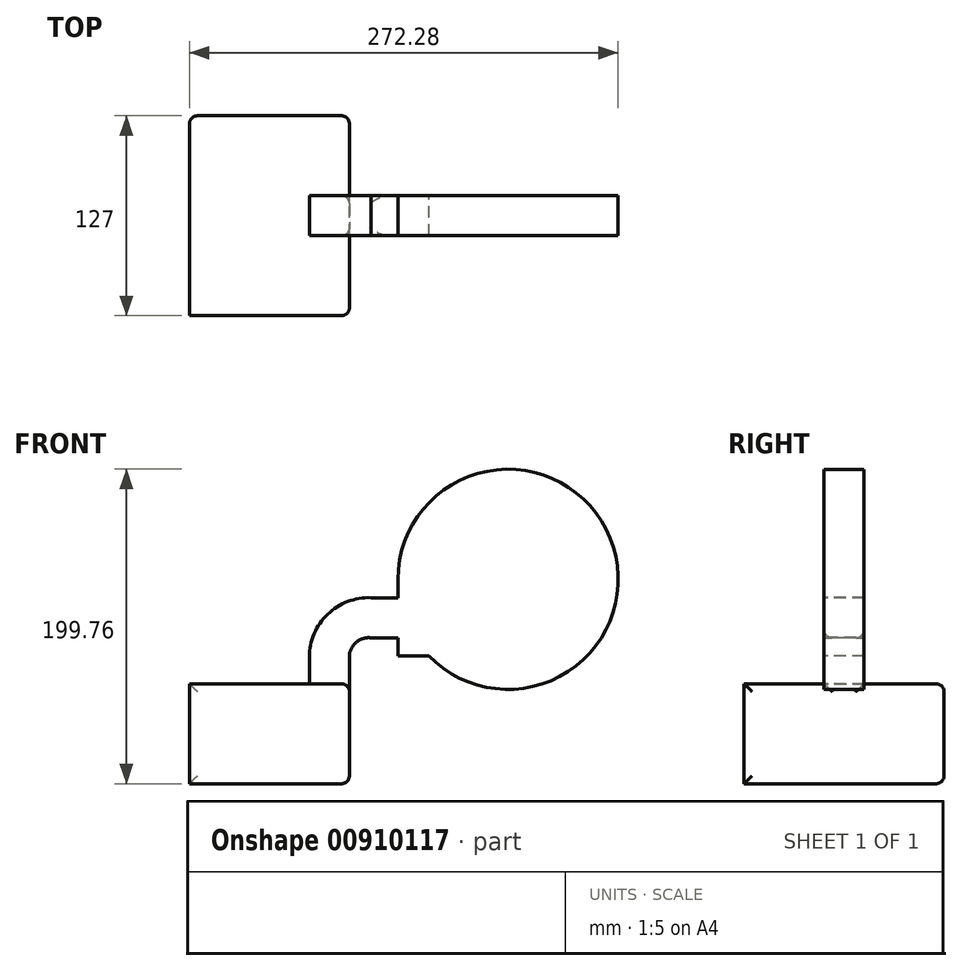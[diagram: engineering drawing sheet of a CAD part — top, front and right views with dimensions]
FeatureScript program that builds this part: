
annotation { "Feature Type Name" : "Feature", "Feature Type Description" : "" }
export const myFeature = defineFeature(function(context is Context, id is Id, definition is map)
    precondition{}
    {
        {
            var Q0;
            Q0=qCreatedBy(makeId("Front.planeOp"),FACE);
            var sketch = newSketch(context, id + "F0", { "sketchPlane" : qUnion([Q0])});
            skLineSegment(sketch, "E0.bottom", {"start": v(-50.8, -31.75) * mm, "end": v(50.8, -31.75) * mm});
            skLineSegment(sketch, "E0.top", {"start": v(-50.8, 31.75) * mm, "end": v(50.8, 31.75) * mm});
            skLineSegment(sketch, "E0.left", {"start": v(-50.8, -31.75) * mm, "end": v(-50.8, 31.75) * mm});
            skLineSegment(sketch, "E0.right", {"start": v(50.8, -31.75) * mm, "end": v(50.8, 31.75) * mm});
            skPoint(sketch, "E0.middle", {"position": v(0, 0) * mm});
            skLineSegment(sketch, "E1.bottom", {"start": v(81.64, 98.09) * mm, "end": v(151.56, 98.09) * mm});
            skLineSegment(sketch, "E1.top", {"start": v(81.64, 49.56) * mm, "end": v(151.56, 49.56) * mm});
            skLineSegment(sketch, "E1.left", {"start": v(81.64, 98.09) * mm, "end": v(81.64, 49.56) * mm});
            skLineSegment(sketch, "E1.right", {"start": v(151.56, 98.09) * mm, "end": v(151.56, 49.56) * mm});
            skPoint(sketch, "E1.middle", {"position": v(116.6, 73.82) * mm});
            skLineSegment(sketch, "E2", {"start": v(50.8, 31.75) * mm, "end": v(50.8, 48.66) * mm});
            skArc(sketch, "E3", {"start": v(50.8, 48.66) * mm, "mid": v(54.72, 57.7) * mm, "end": v(64, 61) * mm});
            skLineSegment(sketch, "E4", {"start": v(64, 61) * mm, "end": v(113.1, 61) * mm});
            skLineSegment(sketch, "E5.0", {"start": v(64.63, 86.4) * mm, "end": v(113.1, 86.4) * mm});
            skArc(sketch, "E5.1", {"start": v(25.4, 48.66) * mm, "mid": v(36.99, 75.87) * mm, "end": v(64.63, 86.4) * mm});
            skLineSegment(sketch, "E5.2", {"start": v(25.4, 31.75) * mm, "end": v(25.4, 48.66) * mm});
            skFitSpline(sketch, "E6", {"points": [v(-50.8, 31.75) * mm, v(64.63, 86.4) * mm], "startDerivative": vector(115.43, 54.64) * mm, "endDerivative": vector(139.56, -16.4) * mm});
            skSolve(sketch);
        }
        {
            var Q0;
            Q0=makeQuery(id+"F0.imprint","IMPRINT",FACE,{"disambiguationData":[TD([[makeQuery(id+"F0.imprint","IMPRINT",EDGE,{"derivedFrom":sQuery(id+"F0.wireOp",EDGE,"E0.bottom")}),1.0]])]});
            extrude(context, id + "F1", {"entities" : qUnion([Q0]), "endBound" : BoundingType.SYMMETRIC, "depth" : 127 * mm, "offsetDistance" : 25.4 * mm});
        }
        {
            var Q0;
            Q0=makeQuery(id+"F0.imprint","IMPRINT",FACE,{"disambiguationData":[TD([[makeQuery(id+"F0.imprint","IMPRINT",EDGE,{"derivedFrom":sQuery(id+"F0.wireOp",EDGE,"E5.1")}),1.0]])]});
            var Q1;
            {var subQ0=sQuery(id+"F0.wireOp",EDGE,"E2");Q1=makeQuery(id+"F0.imprint","IMPRINT",FACE,{"disambiguationData":[TD([[makeQuery(id+"F0.imprint","IMPRINT",EDGE,{"derivedFrom":subQ0}),1.0]])]});}
            var Q2;
            {var subQ3=sQuery(id+"F0.wireOp",EDGE,"E1.bottom");Q2=makeQuery(id+"F0.imprint","IMPRINT",FACE,{"disambiguationData":[TD([[makeQuery(id+"F0.imprint","IMPRINT",EDGE,{"derivedFrom":subQ3}),-1.0]])]});}
            extrude(context, id + "F2", {"entities" : qUnion([Q0, Q1, Q2]), "operationType" : NewBodyOperationType.ADD, "endBound" : BoundingType.SYMMETRIC, "oppositeDirection" : true, "depth" : 25.4 * mm, "offsetDistance" : 25.4 * mm});
        }
        {
            var Q0;
            Q0=makeQuery(id+"F2.opExtrude","SWEPT_FACE",FACE,{"disambiguationData":[OSD([sQuery(id+"F0.wireOp",EDGE,"E1.bottom")])]});
            var Q1;
            Q1=makeQuery(id+"F2.opExtrude","SWEPT_EDGE",EDGE,{"disambiguationData":[OSD([sQuery(id+"F0.wireOp",EDGE,"E1.bottom"),sQuery(id+"F0.wireOp",EDGE,"E1.right")])]});
            revolve(context, id + "F3", {"operationType" : NewBodyOperationType.ADD, "surfaceOperationType" : NewSurfaceOperationType.NEW, "entities" : qUnion([Q0]), "axis" : qUnion([Q1]), "revolveType" : RevolveType.FULL});
        }
        {
            var Q0;
            Q0=makeQuery(id+"F2.boolean.opBoolean","MERGE",FACE,{"derivedFrom":[makeQuery(id+"F1.opExtrude","SWEPT_FACE",FACE,{"disambiguationData":[OSD([sQuery(id+"F0.wireOp",EDGE,"E0.right")])]}),makeQuery(id+"F2.opExtrude","SWEPT_FACE",FACE,{"disambiguationData":[OSD([sQuery(id+"F0.wireOp",EDGE,"E2")])]})]});
            var Q1;
            Q1=makeQuery(id+"F1.opExtrude","CAP_FACE",FACE,{"disambiguationData":[OSD([sQuery(id+"F0.wireOp",EDGE,"E0.bottom"),sQuery(id+"F0.wireOp",EDGE,"E0.top"),sQuery(id+"F0.wireOp",EDGE,"E0.left"),sQuery(id+"F0.wireOp",EDGE,"E0.right")])],"isStart":true});
            fillet(context, id + "F4", {"entities" : qUnion([Q0, Q1]), "radius" : 5.08 * mm, "tangentPropagation" : true, "allowEdgeOverflow" : false});
        }
    });
